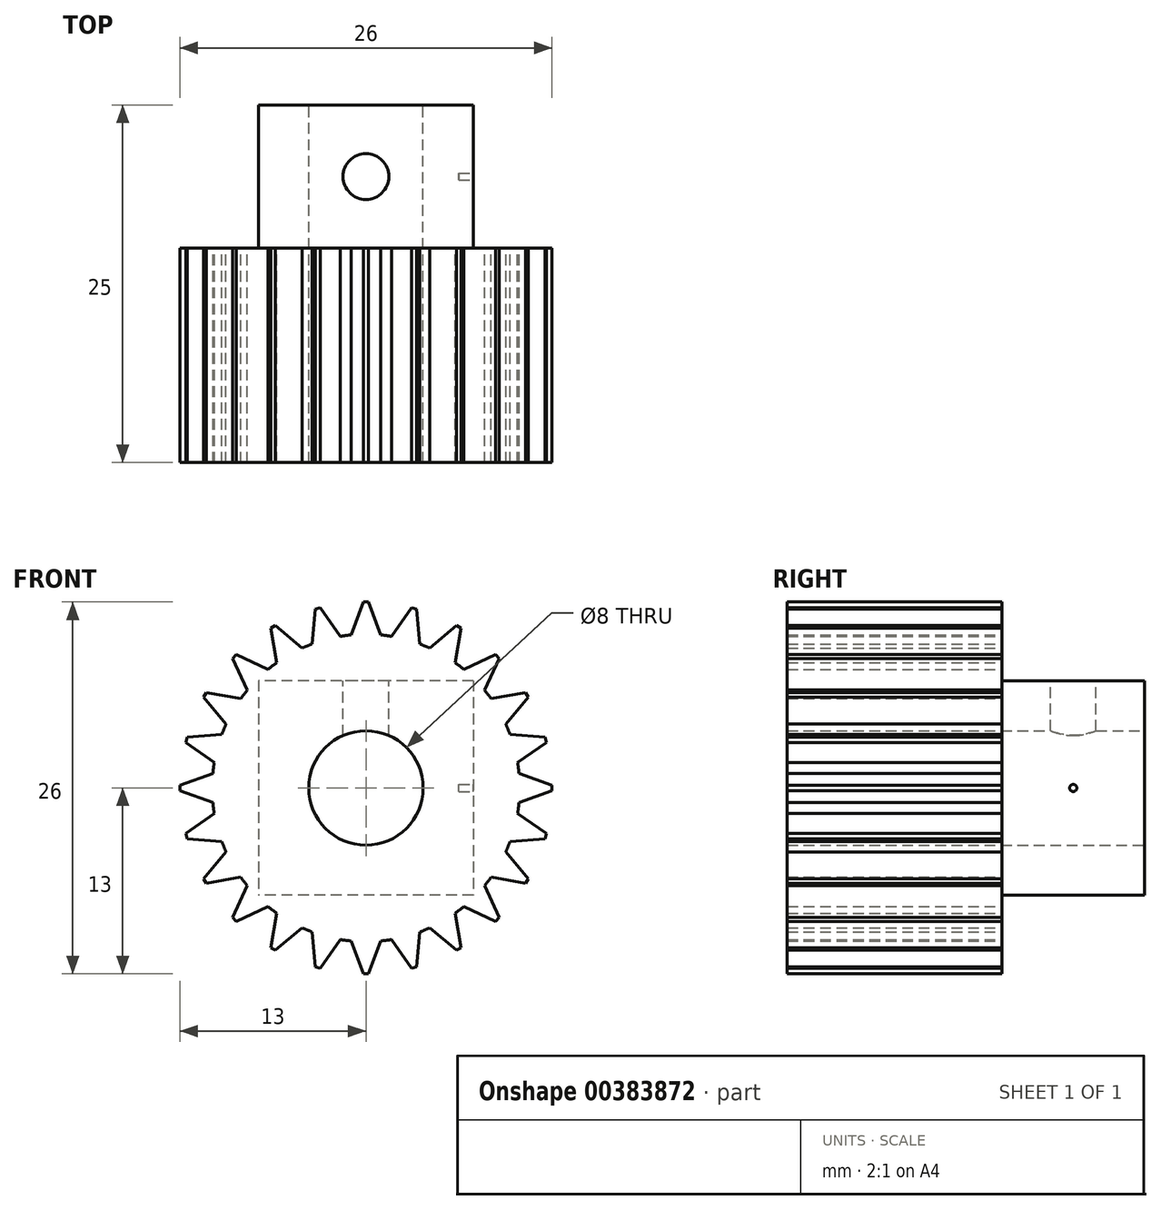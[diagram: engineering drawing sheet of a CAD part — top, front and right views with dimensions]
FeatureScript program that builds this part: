
annotation { "Feature Type Name" : "Feature", "Feature Type Description" : "" }
export const myFeature = defineFeature(function(context is Context, id is Id, definition is map)
    precondition{}
    {
        {
            var Q0;
            Q0=qCreatedBy(makeId("Front.planeOp"),FACE);
            var sketch = newSketch(context, id + "F0", { "sketchPlane" : qUnion([Q0])});
            skCircle(sketch, "E0", {"center": v(0, 0) * mm, "radius": 4 * mm});
            skCircle(sketch, "E1", {"center": v(0, 0) * mm, "radius": 10.75 * mm});
            skCircle(sketch, "E2", {"center": v(0, 0) * mm, "radius": 13 * mm, "construction": true});
            skLineSegment(sketch, "E3", {"start": v(-1.02, 10.7) * mm, "end": v(-0.19, 13) * mm});
            skLineSegment(sketch, "E4", {"start": v(-0.19, 13) * mm, "end": v(0, 13) * mm});
            skLineSegment(sketch, "E5", {"start": v(-1.02, 10.7) * mm, "end": v(-1.02, 13.91) * mm, "construction": true});
            skLineSegment(sketch, "E6.MirrorCS", {"start": v(0.19, 13) * mm, "end": v(0, 13) * mm});
            skLineSegment(sketch, "E7.MirrorCS", {"start": v(1.02, 10.7) * mm, "end": v(0.19, 13) * mm});
            skLineSegment(sketch, "E8.1.0", {"start": v(-3.76, 10.07) * mm, "end": v(-3.55, 12.5) * mm});
            skLineSegment(sketch, "E8.1.1", {"start": v(-3.55, 12.5) * mm, "end": v(-3.36, 12.56) * mm});
            skLineSegment(sketch, "E8.1.2", {"start": v(-3.18, 12.6) * mm, "end": v(-3.36, 12.56) * mm});
            skLineSegment(sketch, "E8.1.3", {"start": v(-1.78, 10.6) * mm, "end": v(-3.18, 12.6) * mm});
            skLineSegment(sketch, "E8.2.0", {"start": v(-6.24, 8.76) * mm, "end": v(-6.66, 11.16) * mm});
            skLineSegment(sketch, "E8.2.1", {"start": v(-6.66, 11.16) * mm, "end": v(-6.5, 11.26) * mm});
            skLineSegment(sketch, "E8.2.2", {"start": v(-6.34, 11.35) * mm, "end": v(-6.5, 11.26) * mm});
            skLineSegment(sketch, "E8.2.3", {"start": v(-4.46, 9.78) * mm, "end": v(-6.34, 11.35) * mm});
            skLineSegment(sketch, "E8.3.0", {"start": v(-8.3, 6.84) * mm, "end": v(-9.32, 9.06) * mm});
            skLineSegment(sketch, "E8.3.1", {"start": v(-9.32, 9.06) * mm, "end": v(-9.2, 9.2) * mm});
            skLineSegment(sketch, "E8.3.2", {"start": v(-9.06, 9.32) * mm, "end": v(-9.2, 9.2) * mm});
            skLineSegment(sketch, "E8.3.3", {"start": v(-6.84, 8.3) * mm, "end": v(-9.06, 9.32) * mm});
            skLineSegment(sketch, "E8.4.0", {"start": v(-9.78, 4.46) * mm, "end": v(-11.35, 6.34) * mm});
            skLineSegment(sketch, "E8.4.1", {"start": v(-11.35, 6.34) * mm, "end": v(-11.26, 6.5) * mm});
            skLineSegment(sketch, "E8.4.2", {"start": v(-11.16, 6.66) * mm, "end": v(-11.26, 6.5) * mm});
            skLineSegment(sketch, "E8.4.3", {"start": v(-8.76, 6.24) * mm, "end": v(-11.16, 6.66) * mm});
            skLineSegment(sketch, "E8.5.0", {"start": v(-10.6, 1.78) * mm, "end": v(-12.6, 3.18) * mm});
            skLineSegment(sketch, "E8.5.1", {"start": v(-12.6, 3.18) * mm, "end": v(-12.56, 3.36) * mm});
            skLineSegment(sketch, "E8.5.2", {"start": v(-12.5, 3.55) * mm, "end": v(-12.56, 3.36) * mm});
            skLineSegment(sketch, "E8.5.3", {"start": v(-10.07, 3.76) * mm, "end": v(-12.5, 3.55) * mm});
            skLineSegment(sketch, "E8.6.0", {"start": v(-10.7, -1.02) * mm, "end": v(-13, -0.19) * mm});
            skLineSegment(sketch, "E8.6.1", {"start": v(-13, -0.19) * mm, "end": v(-13, 0) * mm});
            skLineSegment(sketch, "E8.6.2", {"start": v(-13, 0.19) * mm, "end": v(-13, 0) * mm});
            skLineSegment(sketch, "E8.6.3", {"start": v(-10.7, 1.02) * mm, "end": v(-13, 0.19) * mm});
            skLineSegment(sketch, "E8.7.0", {"start": v(-10.07, -3.76) * mm, "end": v(-12.5, -3.55) * mm});
            skLineSegment(sketch, "E8.7.1", {"start": v(-12.5, -3.55) * mm, "end": v(-12.56, -3.36) * mm});
            skLineSegment(sketch, "E8.7.2", {"start": v(-12.6, -3.18) * mm, "end": v(-12.56, -3.36) * mm});
            skLineSegment(sketch, "E8.7.3", {"start": v(-10.6, -1.78) * mm, "end": v(-12.6, -3.18) * mm});
            skLineSegment(sketch, "E8.8.0", {"start": v(-8.76, -6.24) * mm, "end": v(-11.16, -6.66) * mm});
            skLineSegment(sketch, "E8.8.1", {"start": v(-11.16, -6.66) * mm, "end": v(-11.26, -6.5) * mm});
            skLineSegment(sketch, "E8.8.2", {"start": v(-11.35, -6.34) * mm, "end": v(-11.26, -6.5) * mm});
            skLineSegment(sketch, "E8.8.3", {"start": v(-9.78, -4.46) * mm, "end": v(-11.35, -6.34) * mm});
            skLineSegment(sketch, "E8.9.0", {"start": v(-6.84, -8.3) * mm, "end": v(-9.06, -9.32) * mm});
            skLineSegment(sketch, "E8.9.1", {"start": v(-9.06, -9.32) * mm, "end": v(-9.2, -9.2) * mm});
            skLineSegment(sketch, "E8.9.2", {"start": v(-9.32, -9.06) * mm, "end": v(-9.2, -9.2) * mm});
            skLineSegment(sketch, "E8.9.3", {"start": v(-8.3, -6.84) * mm, "end": v(-9.32, -9.06) * mm});
            skLineSegment(sketch, "E8.10.0", {"start": v(-4.46, -9.78) * mm, "end": v(-6.34, -11.35) * mm});
            skLineSegment(sketch, "E8.10.1", {"start": v(-6.34, -11.35) * mm, "end": v(-6.5, -11.26) * mm});
            skLineSegment(sketch, "E8.10.2", {"start": v(-6.66, -11.16) * mm, "end": v(-6.5, -11.26) * mm});
            skLineSegment(sketch, "E8.10.3", {"start": v(-6.24, -8.76) * mm, "end": v(-6.66, -11.16) * mm});
            skLineSegment(sketch, "E8.11.0", {"start": v(-1.78, -10.6) * mm, "end": v(-3.18, -12.6) * mm});
            skLineSegment(sketch, "E8.11.1", {"start": v(-3.18, -12.6) * mm, "end": v(-3.36, -12.56) * mm});
            skLineSegment(sketch, "E8.11.2", {"start": v(-3.55, -12.5) * mm, "end": v(-3.36, -12.56) * mm});
            skLineSegment(sketch, "E8.11.3", {"start": v(-3.76, -10.07) * mm, "end": v(-3.55, -12.5) * mm});
            skLineSegment(sketch, "E9.1.12.0", {"start": v(1.02, -10.7) * mm, "end": v(0.19, -13) * mm});
            skLineSegment(sketch, "E9.3.12.0", {"start": v(0.19, -13) * mm, "end": v(0, -13) * mm});
            skLineSegment(sketch, "E9.6.12.0", {"start": v(-0.19, -13) * mm, "end": v(0, -13) * mm});
            skLineSegment(sketch, "E9.9.12.0", {"start": v(-1.02, -10.7) * mm, "end": v(-0.19, -13) * mm});
            skLineSegment(sketch, "E9.1.13.0", {"start": v(3.76, -10.07) * mm, "end": v(3.55, -12.5) * mm});
            skLineSegment(sketch, "E9.3.13.0", {"start": v(3.55, -12.5) * mm, "end": v(3.36, -12.56) * mm});
            skLineSegment(sketch, "E9.6.13.0", {"start": v(3.18, -12.6) * mm, "end": v(3.36, -12.56) * mm});
            skLineSegment(sketch, "E9.9.13.0", {"start": v(1.78, -10.6) * mm, "end": v(3.18, -12.6) * mm});
            skLineSegment(sketch, "E9.1.14.0", {"start": v(6.24, -8.76) * mm, "end": v(6.66, -11.16) * mm});
            skLineSegment(sketch, "E9.3.14.0", {"start": v(6.66, -11.16) * mm, "end": v(6.5, -11.26) * mm});
            skLineSegment(sketch, "E9.6.14.0", {"start": v(6.34, -11.35) * mm, "end": v(6.5, -11.26) * mm});
            skLineSegment(sketch, "E9.9.14.0", {"start": v(4.46, -9.78) * mm, "end": v(6.34, -11.35) * mm});
            skLineSegment(sketch, "E9.1.15.0", {"start": v(8.3, -6.84) * mm, "end": v(9.32, -9.06) * mm});
            skLineSegment(sketch, "E9.3.15.0", {"start": v(9.32, -9.06) * mm, "end": v(9.2, -9.2) * mm});
            skLineSegment(sketch, "E9.6.15.0", {"start": v(9.06, -9.32) * mm, "end": v(9.2, -9.2) * mm});
            skLineSegment(sketch, "E9.9.15.0", {"start": v(6.84, -8.3) * mm, "end": v(9.06, -9.32) * mm});
            skLineSegment(sketch, "E9.1.16.0", {"start": v(9.78, -4.46) * mm, "end": v(11.35, -6.34) * mm});
            skLineSegment(sketch, "E9.3.16.0", {"start": v(11.35, -6.34) * mm, "end": v(11.26, -6.5) * mm});
            skLineSegment(sketch, "E9.6.16.0", {"start": v(11.16, -6.66) * mm, "end": v(11.26, -6.5) * mm});
            skLineSegment(sketch, "E9.9.16.0", {"start": v(8.76, -6.24) * mm, "end": v(11.16, -6.66) * mm});
            skLineSegment(sketch, "E9.1.17.0", {"start": v(10.6, -1.78) * mm, "end": v(12.6, -3.18) * mm});
            skLineSegment(sketch, "E9.3.17.0", {"start": v(12.6, -3.18) * mm, "end": v(12.56, -3.36) * mm});
            skLineSegment(sketch, "E9.6.17.0", {"start": v(12.5, -3.55) * mm, "end": v(12.56, -3.36) * mm});
            skLineSegment(sketch, "E9.9.17.0", {"start": v(10.07, -3.76) * mm, "end": v(12.5, -3.55) * mm});
            skLineSegment(sketch, "E9.1.18.0", {"start": v(10.7, 1.02) * mm, "end": v(13, 0.19) * mm});
            skLineSegment(sketch, "E9.3.18.0", {"start": v(13, 0.19) * mm, "end": v(13, 0) * mm});
            skLineSegment(sketch, "E9.6.18.0", {"start": v(13, -0.19) * mm, "end": v(13, 0) * mm});
            skLineSegment(sketch, "E9.9.18.0", {"start": v(10.7, -1.02) * mm, "end": v(13, -0.19) * mm});
            skLineSegment(sketch, "E9.1.19.0", {"start": v(10.07, 3.76) * mm, "end": v(12.5, 3.55) * mm});
            skLineSegment(sketch, "E9.3.19.0", {"start": v(12.5, 3.55) * mm, "end": v(12.56, 3.36) * mm});
            skLineSegment(sketch, "E9.6.19.0", {"start": v(12.6, 3.18) * mm, "end": v(12.56, 3.36) * mm});
            skLineSegment(sketch, "E9.9.19.0", {"start": v(10.6, 1.78) * mm, "end": v(12.6, 3.18) * mm});
            skLineSegment(sketch, "E9.1.20.0", {"start": v(8.76, 6.24) * mm, "end": v(11.16, 6.66) * mm});
            skLineSegment(sketch, "E9.3.20.0", {"start": v(11.16, 6.66) * mm, "end": v(11.26, 6.5) * mm});
            skLineSegment(sketch, "E9.6.20.0", {"start": v(11.35, 6.34) * mm, "end": v(11.26, 6.5) * mm});
            skLineSegment(sketch, "E9.9.20.0", {"start": v(9.78, 4.46) * mm, "end": v(11.35, 6.34) * mm});
            skLineSegment(sketch, "E9.1.21.0", {"start": v(6.84, 8.3) * mm, "end": v(9.06, 9.32) * mm});
            skLineSegment(sketch, "E9.3.21.0", {"start": v(9.06, 9.32) * mm, "end": v(9.2, 9.2) * mm});
            skLineSegment(sketch, "E9.6.21.0", {"start": v(9.32, 9.06) * mm, "end": v(9.2, 9.2) * mm});
            skLineSegment(sketch, "E9.9.21.0", {"start": v(8.3, 6.84) * mm, "end": v(9.32, 9.06) * mm});
            skLineSegment(sketch, "E9.1.22.0", {"start": v(4.46, 9.78) * mm, "end": v(6.34, 11.35) * mm});
            skLineSegment(sketch, "E9.3.22.0", {"start": v(6.34, 11.35) * mm, "end": v(6.5, 11.26) * mm});
            skLineSegment(sketch, "E9.6.22.0", {"start": v(6.66, 11.16) * mm, "end": v(6.5, 11.26) * mm});
            skLineSegment(sketch, "E9.9.22.0", {"start": v(6.24, 8.76) * mm, "end": v(6.66, 11.16) * mm});
            skLineSegment(sketch, "E9.1.23.0", {"start": v(1.78, 10.6) * mm, "end": v(3.18, 12.6) * mm});
            skLineSegment(sketch, "E9.3.23.0", {"start": v(3.18, 12.6) * mm, "end": v(3.36, 12.56) * mm});
            skLineSegment(sketch, "E9.6.23.0", {"start": v(3.55, 12.5) * mm, "end": v(3.36, 12.56) * mm});
            skLineSegment(sketch, "E9.9.23.0", {"start": v(3.76, 10.07) * mm, "end": v(3.55, 12.5) * mm});
            skSolve(sketch);
        }
        {
            var Q0;
            Q0=qSketchRegion(id+"F0",true);
            extrude(context, id + "F1", {"entities" : qUnion([Q0]), "depth" : 15 * mm});
        }
        {
            var Q0;
            Q0=qCreatedBy(makeId("Front.planeOp"),FACE);
            var sketch = newSketch(context, id + "F2", { "sketchPlane" : qUnion([Q0])});
            skCircle(sketch, "E10", {"center": v(0, 0) * mm, "radius": 4 * mm});
            skLineSegment(sketch, "E11.bottom", {"start": v(7.5, 7.5) * mm, "end": v(-7.5, 7.5) * mm});
            skLineSegment(sketch, "E11.top", {"start": v(7.5, -7.5) * mm, "end": v(-7.5, -7.5) * mm});
            skLineSegment(sketch, "E11.left", {"start": v(7.5, 7.5) * mm, "end": v(7.5, -7.5) * mm});
            skLineSegment(sketch, "E11.right", {"start": v(-7.5, 7.5) * mm, "end": v(-7.5, -7.5) * mm});
            skSolve(sketch);
        }
        {
            var Q0;
            Q0 = qSketchRegion(id + "F2", true);
            extrude(context, id + "F3", {"entities" : qUnion([Q0]), "operationType" : NewBodyOperationType.ADD, "depth" : -10 * mm});
        }
        {
            var Q0;
            Q0=makeQuery(id+"F3.opExtrude","SWEPT_FACE",FACE,{"disambiguationData":[OSD([sQuery(id+"F2.wireOp",EDGE,"E11.bottom")])]});
            var sketch = newSketch(context, id + "F4", { "sketchPlane" : qUnion([Q0])});
            skLineSegment(sketch, "E12", {"start": v(0, 0) * mm, "end": v(0, 5) * mm, "construction": true});
            skCircle(sketch, "E13", {"center": v(0, 5) * mm, "radius": 1.6 * mm});
            skSolve(sketch);
        }
        {
            var Q0;
            Q0 = qSketchRegion(id + "F4", true);
            var Q1;
            Q1=makeQuery(id+"F3.boolean.opBoolean","MERGE",FACE,{"derivedFrom":[makeQuery(id+"F1.opExtrude","SWEPT_FACE",FACE,{"disambiguationData":[OSD([sQuery(id+"F0.wireOp",EDGE,"E0")])]}),makeQuery(id+"F3.opExtrude","SWEPT_FACE",FACE,{"disambiguationData":[OSD([sQuery(id+"F2.wireOp",EDGE,"E10")])]})]});
            extrude(context, id + "F5", {"entities" : qUnion([Q0]), "operationType" : NewBodyOperationType.REMOVE, "endBound" : BoundingType.UP_TO_SURFACE, "oppositeDirection" : true, "endBoundEntityFace" : qUnion([Q1]), "depth" : 25 * mm});
        }
        {
            var Q0;
            Q0=makeQuery(id+"F3.opExtrude","SWEPT_FACE",FACE,{"disambiguationData":[OSD([sQuery(id+"F2.wireOp",EDGE,"E11.left")])]});
            var sketch = newSketch(context, id + "F6", { "sketchPlane" : qUnion([Q0])});
            skPoint(sketch, "E14.endSnap0", {"position": v(0, 0) * mm});
            skLineSegment(sketch, "E15", {"start": v(0, 0) * mm, "end": v(5, 0) * mm, "construction": true});
            skLineSegment(sketch, "E16", {"start": v(5, 7.5) * mm, "end": v(5, 0) * mm, "construction": true});
            skCircle(sketch, "E17", {"center": v(5, 0) * mm, "radius": 0.25 * mm});
            skSolve(sketch);
        }
        {
            var Q0;
            Q0 = qSketchRegion(id + "F6", true);
            extrude(context, id + "F7", {"entities" : qUnion([Q0]), "depth" : -1 * mm});
        }
    });
